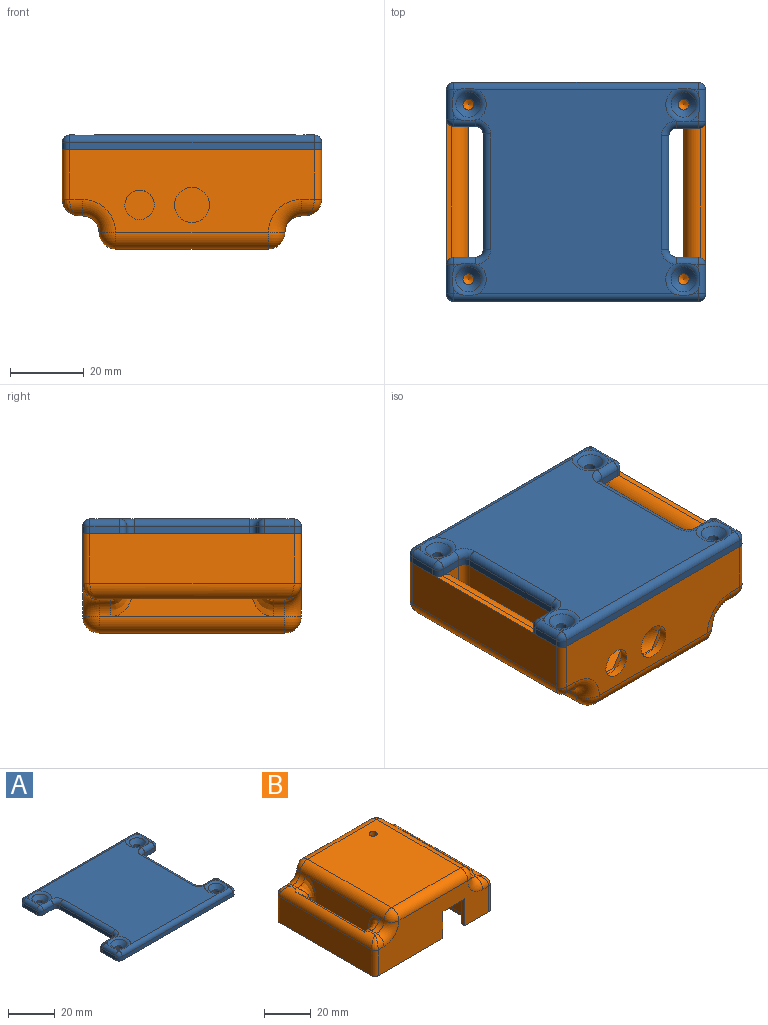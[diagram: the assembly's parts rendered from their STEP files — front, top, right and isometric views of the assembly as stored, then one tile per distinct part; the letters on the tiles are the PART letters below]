
ASSEMBLY  parts=2 mates=1
PART A: 75 faces, bbox 72x61x4 mm
  f0: plane 1.3x1.3mm, normal (0,0,1), area 0.7mm2, adj f72,f73,f74
  f1: plane 1.3x1.3mm, normal (0,0,1), area 0.7mm2, adj f71,f72,f74
  f2: plane 1.3x1.3mm, normal (0,0,1), area 0.7mm2, adj f37,f42,f47
  f3: plane 1.3x1.3mm, normal (0,0,1), area 0.7mm2, adj f37,f41,f42
  f4: plane 1.3x1.3mm, normal (0,0,1), area 0.7mm2, adj f47,f48,f53
  f5: plane 1.3x1.3mm, normal (0,0,1), area 0.7mm2, adj f48,f53,f54
  f6: plane 1.3x1.3mm, normal (0,0,1), area 0.7mm2, adj f62,f69,f73
  f7: plane 2.25x1.8mm, normal (0,0,1), area 1.6mm2, adj f62,f63,f69
  f8: plane 8x2mm, normal (-1,0,0), area 16mm2, adj f21,f39,f45,f48
  f9: plane 66.5x2mm, normal (0,-1,0), area 133mm2, adj f21,f38,f39,f47
  f10: plane 8x2mm, normal (1,0,0), area 16mm2, adj f21,f35,f37,f38
  f11: plane 6x2mm, normal (0,1,0), area 12mm2, adj f21,f35,f40,f41
  f12: plane 31x2mm, normal (1,0,0), area 62mm2, adj f21,f40,f51,f52
  f13: plane 6x2mm, normal (0,-1,0), area 12mm2, adj f21,f50,f51,f63
  f14: plane 8.5x2mm, normal (1,0,0), area 17mm2, adj f21,f50,f61,f62
  f15: plane 66.5x2mm, normal (0,1,0), area 133mm2, adj f21,f60,f61,f73
  f16: plane 8x2mm, normal (-1,0,0), area 16mm2, adj f21,f59,f60,f72
  f17: plane 6x2mm, normal (0,-1,0), area 12mm2, adj f21,f59,f65,f71
  f18: plane 31.5x2mm, normal (-1,0,0), area 63mm2, adj f21,f55,f64,f65
  f19: plane 6x2mm, normal (0,1,0), area 12mm2, adj f21,f45,f54,f55
  f20: plane 55.5x54.12mm, normal (0,0,1), area 2654mm2, adj f42,f46,f47,f52,f53,f57,f58,f63
  f21: plane 70.5x59.5mm, normal (0,0,-1), area 970.3mm2, adj f8,f9,f10,f11,f12,f13,f14,f15
  f22: cylinder r=1.5mm len=3mm, axis (0,0,1), area 14.1mm2, adj f21,f23
  f23: cone r=1.5mm half-angle=45deg, axis (0,0,1), area 41.8mm2, adj f22,f53
  f24: cylinder r=1.5mm len=3mm, axis (0,0,1), area 14.1mm2, adj f21,f25
  f25: cone r=1.5mm half-angle=45deg, axis (0,0,1), area 41.8mm2, adj f24,f42
  f26: cylinder r=1.5mm len=3mm, axis (0,0,1), area 14.1mm2, adj f21,f27
  f27: cone r=1.5mm half-angle=45deg, axis (0,0,1), area 41.8mm2, adj f26,f69
  f28: cylinder r=1.5mm len=3mm, axis (0,0,1), area 14.1mm2, adj f21,f29
  f29: cone r=1.5mm half-angle=45deg, axis (0,0,1), area 41.8mm2, adj f28,f74
  f30: plane 46.5x2mm, normal (0,-1,0), area 93mm2, adj f21,f31,f33,f34
  f31: plane 53.5x2mm, normal (1,0,0), area 107mm2, adj f21,f30,f32,f34
  f32: plane 46.5x2mm, normal (0,1,0), area 93mm2, adj f21,f31,f33,f34
  f33: plane 53.5x2mm, normal (-1,0,0), area 107mm2, adj f21,f30,f32,f34
  f34: plane 53.5x46.5mm, normal (0,0,-1), area 2487.7mm2, adj f30,f31,f32,f33
  f35: cylinder r=2mm len=2mm, axis (0,0,-1), area 6.3mm2, adj f10,f11,f21,f36
  f36: sphere r=2mm, area 6.3mm2, adj f35,f37,f41
  f37: cylinder r=2mm len=8mm, axis (0,-1,0), area 24mm2, adj f2,f3,f10,f36,f42,f43
  f38: cylinder r=2mm len=2mm, axis (0,0,-1), area 6.3mm2, adj f9,f10,f21,f43
  f39: cylinder r=2mm len=2mm, axis (0,0,1), area 6.3mm2, adj f8,f9,f21,f44
  f40: cylinder r=2mm len=2mm, axis (0,0,-1), area 6.3mm2, adj f11,f12,f21,f46
  f41: cylinder r=2mm len=6mm, axis (1,0,0), area 17.4mm2, adj f3,f11,f36,f42,f46
  f42: torus R=4.83mm, axis (0,0,1), area 36mm2, adj f2,f3,f20,f25,f37,f41,f46,f47
  f43: sphere r=2mm, area 6.3mm2, adj f37,f38,f47
  f44: sphere r=2mm, area 6.3mm2, adj f39,f47,f48
  f45: cylinder r=2mm len=2mm, axis (0,0,1), area 6.3mm2, adj f8,f19,f21,f49
  f46: torus R=4mm, axis (0,0,1), area 13.4mm2, adj f20,f40,f41,f42,f52
  f47: cylinder r=2mm len=66.5mm, axis (-1,0,0), area 205.9mm2, adj f2,f4,f9,f20,f42,f43,f44,f53
  f48: cylinder r=2mm len=8mm, axis (0,1,0), area 23.6mm2, adj f4,f5,f8,f44,f49,f53
  f49: sphere r=2mm, area 6.3mm2, adj f45,f48,f54
  f50: cylinder r=2mm len=2mm, axis (0,0,-1), area 6.3mm2, adj f13,f14,f21,f56
  f51: cylinder r=2mm len=2mm, axis (0,0,1), area 6.3mm2, adj f12,f13,f21,f57
  f52: cylinder r=2mm len=31mm, axis (0,-1,0), area 97.4mm2, adj f12,f20,f46,f57
  f53: torus R=4.83mm, axis (0,0,1), area 35.6mm2, adj f4,f5,f20,f23,f47,f48,f54,f58
  f54: cylinder r=2mm len=6mm, axis (1,0,0), area 17.4mm2, adj f5,f19,f49,f53,f58
  f55: cylinder r=2mm len=2mm, axis (0,0,1), area 6.3mm2, adj f18,f19,f21,f58
  f56: sphere r=2mm, area 6.3mm2, adj f50,f62,f63
  f57: torus R=4mm, axis (0,0,1), area 13.5mm2, adj f20,f51,f52,f63
  f58: torus R=4mm, axis (0,0,1), area 13.4mm2, adj f20,f53,f54,f55,f64
  f59: cylinder r=2mm len=2mm, axis (0,0,1), area 6.3mm2, adj f16,f17,f21,f66
  f60: cylinder r=2mm len=2mm, axis (0,0,1), area 6.3mm2, adj f15,f16,f21,f67
  f61: cylinder r=2mm len=2mm, axis (0,0,-1), area 6.3mm2, adj f14,f15,f21,f68
  f62: cylinder r=2mm len=8.5mm, axis (0,-1,0), area 25.6mm2, adj f6,f7,f14,f56,f68,f69
  f63: cylinder r=2mm len=6mm, axis (-1,0,0), area 18.5mm2, adj f7,f13,f20,f56,f57,f69
  f64: cylinder r=2mm len=31.5mm, axis (0,1,0), area 99mm2, adj f18,f20,f58,f70
  f65: cylinder r=2mm len=2mm, axis (0,0,-1), area 6.3mm2, adj f17,f18,f21,f70
  f66: sphere r=2mm, area 6.3mm2, adj f59,f71,f72
  f67: sphere r=2mm, area 6.3mm2, adj f60,f72,f73
  f68: sphere r=2mm, area 6.3mm2, adj f61,f62,f73
  f69: torus R=4.83mm, axis (0,0,1), area 37.2mm2, adj f6,f7,f20,f27,f62,f63,f73
  f70: torus R=4mm, axis (0,0,1), area 13.4mm2, adj f20,f64,f65,f71,f74
  f71: cylinder r=2mm len=6mm, axis (-1,0,0), area 17.4mm2, adj f1,f17,f66,f70,f74
  f72: cylinder r=2mm len=8mm, axis (0,1,0), area 23.6mm2, adj f0,f1,f16,f66,f67,f74
  f73: cylinder r=2mm len=66.5mm, axis (1,0,0), area 205.9mm2, adj f0,f6,f15,f20,f67,f68,f69,f74
  f74: torus R=4.83mm, axis (0,0,1), area 35.6mm2, adj f0,f1,f20,f29,f70,f71,f72,f73
PART B: 123 faces, bbox 70.9x62.5x27.4 mm
  f0: plane 6x2.29mm, normal (0,0,-1), area 4.3mm2, adj f100,f110,f116
  f1: plane 44.5x24mm, normal (0,-1,0), area 796.4mm2, adj f20,f38,f39,f40,f41,f42,f43,f45
  f2: plane 51.5x2mm, normal (-1,0,0), area 103mm2, adj f20,f104,f121,f122
  f3: plane 51.5x2mm, normal (1,0,0), area 103mm2, adj f20,f102,f119,f120
  f4: plane 44.5x24mm, normal (0,1,0), area 842mm2, adj f20,f34,f35,f36,f102,f104,f105,f106
  f5: plane 3x1mm, normal (0,0,1), area 3mm2, adj f60,f63,f66,f72
  f6: plane 3x1mm, normal (0,0,1), area 3mm2, adj f78,f79,f89,f90
  f7: plane 13.5x6.5mm, normal (0,-1,0), area 31.3mm2, adj f20,f33,f52,f64,f95
  f8: plane 13.5x6.5mm, normal (0,1,0), area 31.3mm2, adj f20,f31,f56,f78,f96
  f9: plane 55.5x13.5mm, normal (1,0,0), area 749.2mm2, adj f20,f55,f58,f79
  f10: plane 66.5x22.5mm, normal (0,1,0), area 1184.9mm2, adj f16,f17,f20,f51,f58,f65,f69,f75
  f11: plane 13.5x6.5mm, normal (0,1,0), area 31.3mm2, adj f20,f33,f53,f63,f95
  f12: plane 55.5x13.5mm, normal (-1,0,0), area 749.2mm2, adj f20,f51,f54,f60
  f13: plane 66.5x22.5mm, normal (0,-1,0), area 1124mm2, adj f20,f34,f35,f36,f54,f55,f66,f71
  f14: plane 13.5x6.5mm, normal (0,-1,0), area 31.3mm2, adj f20,f31,f57,f77,f96
  f15: plane 50.5x41.5mm, normal (0,0,1), area 2086.1mm2, adj f80,f81,f91,f92,f97
  f16: cylinder r=4.75mm len=9.5mm, axis (0,1,0), area 59.7mm2, adj f10,f44
  f17: cylinder r=4mm len=8mm, axis (0,1,0), area 50.3mm2, adj f10,f37
  f18: plane 44.89x22.89mm, normal (-1,0,0), area 732.3mm2, adj f20,f52,f53,f67,f68,f80
  f19: plane 44.89x22.89mm, normal (1,0,0), area 731.3mm2, adj f20,f56,f57,f83,f84,f92
  f20: plane 70.5x59.5mm, normal (0,0,-1), area 1050.1mm2, adj f1,f2,f3,f4,f7,f8,f9,f10
  f21: plane 51.5x42.5mm, normal (0,0,-1), area 1957.8mm2, adj f100,f107,f110,f113,f117
  f22: cone r=0mm half-angle=59deg, axis (0,0,-1), area 8.2mm2, adj f23
  f23: cylinder r=1.5mm len=10mm, axis (0,0,-1), area 94.2mm2, adj f20,f22
  f24: cone r=0mm half-angle=59deg, axis (0,0,-1), area 8.2mm2, adj f25
  f25: cylinder r=1.5mm len=10mm, axis (0,0,-1), area 94.2mm2, adj f20,f24
  f26: cone r=0mm half-angle=59deg, axis (0,0,-1), area 8.2mm2, adj f27
  f27: cylinder r=1.5mm len=10mm, axis (0,0,-1), area 94.2mm2, adj f20,f26
  f28: cone r=0mm half-angle=59deg, axis (0,0,-1), area 8.2mm2, adj f29
  f29: cylinder r=1.5mm len=10mm, axis (0,0,-1), area 94.2mm2, adj f20,f28
  f30: plane 3x1mm, normal (0,0,1), area 3mm2, adj f75,f77,f79,f88
  f31: plane 35.5x9mm, normal (-1,0,0), area 319.5mm2, adj f8,f14,f76,f96
  f32: plane 3x1mm, normal (0,0,1), area 3mm2, adj f60,f64,f65,f73
  f33: plane 35.5x9mm, normal (1,0,0), area 319.5mm2, adj f7,f11,f59,f95
  f34: plane 14x2mm, normal (-1,0,0), area 28mm2, adj f4,f13,f20,f35
  f35: plane 13x2mm, normal (0,0,-1), area 26mm2, adj f4,f13,f34,f36
  f36: plane 14x2mm, normal (1,0,0), area 28mm2, adj f4,f13,f20,f35
  f37: plane 11.78x10.2mm, normal (0,-1,0), area 39.8mm2, adj f17,f38,f39,f40,f41,f42,f43
  f38: plane 5.1x2.94mm, normal (0.87,0,0.5), area 11.8mm2, adj f1,f37,f39,f43
  f39: plane 5.89x2mm, normal (0,0,1), area 11.8mm2, adj f1,f37,f38,f40
  f40: plane 5.1x2.94mm, normal (-0.87,0,0.5), area 11.8mm2, adj f1,f37,f39,f41
  f41: plane 5.1x2.94mm, normal (-0.87,0,-0.5), area 11.8mm2, adj f1,f37,f40,f42
  f42: plane 5.89x2mm, normal (0,0,-1), area 11.8mm2, adj f1,f37,f41,f43
  f43: plane 5.1x2.94mm, normal (0.87,0,-0.5), area 11.8mm2, adj f1,f37,f38,f42
  f44: plane 14.09x12.2mm, normal (0,-1,0), area 58mm2, adj f16,f45,f46,f47,f48,f49,f50
  f45: plane 6.1x3.52mm, normal (0.87,0,0.5), area 14.1mm2, adj f1,f44,f46,f50
  f46: plane 7.04x2mm, normal (0,0,1), area 14.1mm2, adj f1,f44,f45,f47
  f47: plane 6.1x3.52mm, normal (-0.87,0,0.5), area 14.1mm2, adj f1,f44,f46,f48
  f48: plane 6.1x3.52mm, normal (-0.87,0,-0.5), area 14.1mm2, adj f1,f44,f47,f49
  f49: plane 7.04x2mm, normal (0,0,-1), area 14.1mm2, adj f1,f44,f48,f50
  f50: plane 6.1x3.52mm, normal (0.87,0,-0.5), area 14.1mm2, adj f1,f44,f45,f49
  f51: cylinder r=2mm len=13.5mm, axis (0,0,1), area 42.4mm2, adj f10,f12,f20,f61
  f52: cylinder r=2mm len=13.5mm, axis (0,0,1), area 42.4mm2, adj f7,f18,f20,f68
  f53: cylinder r=2mm len=13.5mm, axis (0,0,-1), area 42.4mm2, adj f11,f18,f20,f67
  f54: cylinder r=2mm len=13.5mm, axis (0,0,-1), area 42.4mm2, adj f12,f13,f20,f62
  f55: cylinder r=2mm len=13.5mm, axis (0,0,-1), area 42.4mm2, adj f9,f13,f20,f85
  f56: cylinder r=2mm len=13.5mm, axis (0,0,-1), area 42.4mm2, adj f8,f19,f20,f84
  f57: cylinder r=2mm len=13.5mm, axis (0,0,1), area 42.4mm2, adj f14,f19,f20,f83
  f58: cylinder r=2mm len=13.5mm, axis (0,0,1), area 42.4mm2, adj f9,f10,f20,f70
  f59: cylinder r=4.5mm len=41.5mm, axis (0,-1,0), area 213.3mm2, adj f33,f60,f63,f64
  f60: cylinder r=4.5mm len=55.5mm, axis (0,1,0), area 308.9mm2, adj f5,f12,f32,f59,f61,f62,f63,f64
  f61: bspline ~4.71x4.5mm, area 9.8mm2, adj f51,f60,f65
  f62: bspline ~4.71x4.5mm, area 9.8mm2, adj f54,f60,f66
  f63: cylinder r=4.5mm len=5mm, axis (1,0,0), area 14.6mm2, adj f5,f11,f59,f60,f67
  f64: cylinder r=4.5mm len=5mm, axis (-1,0,0), area 14.6mm2, adj f7,f32,f59,f60,f68
  f65: cylinder r=4.5mm len=4.5mm, axis (1,0,0), area 18.3mm2, adj f10,f32,f61,f69
  f66: cylinder r=4.5mm len=4.5mm, axis (-1,0,0), area 18.3mm2, adj f5,f13,f62,f71
  f67: bspline ~9x6.5mm, area 45.2mm2, adj f18,f53,f63,f72
  f68: bspline ~9x6.5mm, area 45.2mm2, adj f18,f52,f64,f73
  f69: torus R=9mm, axis (0,-1,0), area 68.1mm2, adj f10,f65,f73,f74
  f70: bspline ~4.71x4.5mm, area 9.8mm2, adj f58,f75,f79
  f71: torus R=9mm, axis (0,-1,0), area 68.1mm2, adj f13,f66,f72,f86
  f72: cylinder r=4.5mm len=4.5mm, axis (0,-1,0), area 21.2mm2, adj f5,f67,f71,f80
  f73: cylinder r=4.5mm len=4.5mm, axis (0,1,0), area 21.2mm2, adj f32,f68,f69,f80
  f74: sphere r=4.5mm, area 43.4mm2, adj f69,f80,f81
  f75: cylinder r=4.5mm len=4.5mm, axis (1,0,0), area 18.3mm2, adj f10,f30,f70,f82
  f76: cylinder r=4.5mm len=41.5mm, axis (0,-1,0), area 213.3mm2, adj f31,f77,f78,f79
  f77: cylinder r=4.5mm len=5mm, axis (-1,0,0), area 14.6mm2, adj f14,f30,f76,f79,f83
  f78: cylinder r=4.5mm len=5mm, axis (1,0,0), area 14.6mm2, adj f6,f8,f76,f79,f84
  f79: cylinder r=4.5mm len=55.5mm, axis (0,1,0), area 308.9mm2, adj f6,f9,f30,f70,f76,f77,f78,f85
  f80: cylinder r=4.5mm len=50.5mm, axis (0,1,0), area 357mm2, adj f15,f18,f72,f73,f74,f86
  f81: cylinder r=4.5mm len=41.5mm, axis (1,0,0), area 293.3mm2, adj f10,f15,f74,f87
  f82: torus R=9mm, axis (0,-1,0), area 68.1mm2, adj f10,f75,f87,f88
  f83: bspline ~9x6.5mm, area 45.2mm2, adj f19,f57,f77,f88
  f84: bspline ~9x6.5mm, area 45.2mm2, adj f19,f56,f78,f89
  f85: bspline ~4.71x4.5mm, area 9.8mm2, adj f55,f79,f90
  f86: sphere r=4.5mm, area 31.8mm2, adj f71,f80,f91
  f87: sphere r=4.5mm, area 20.2mm2, adj f81,f82,f92
  f88: cylinder r=4.5mm len=4.5mm, axis (0,-1,0), area 21.2mm2, adj f30,f82,f83,f92
  f89: cylinder r=4.5mm len=4.5mm, axis (0,1,0), area 21.2mm2, adj f6,f84,f92,f93
  f90: cylinder r=4.5mm len=4.5mm, axis (-1,0,0), area 18.3mm2, adj f6,f13,f85,f93
  f91: cylinder r=4.5mm len=41.5mm, axis (-1,0,0), area 293.3mm2, adj f13,f15,f86,f94
  f92: cylinder r=4.5mm len=50.5mm, axis (0,-1,0), area 357mm2, adj f15,f19,f87,f88,f89,f94
  f93: torus R=9mm, axis (0,-1,0), area 68.1mm2, adj f13,f89,f90,f94
  f94: sphere r=4.5mm, area 31.8mm2, adj f91,f92,f93
  f95: cylinder r=4.5mm len=35.5mm, axis (0,1,0), area 250.9mm2, adj f7,f11,f20,f33
  f96: cylinder r=4.5mm len=35.5mm, axis (0,1,0), area 250.9mm2, adj f8,f14,f20,f31
  f97: cylinder r=1.75mm len=17mm, axis (0,0,1), area 186.9mm2, adj f15,f99
  f98: cylinder r=4mm len=10mm, axis (0,0,1), area 251.3mm2, adj f99,f100
  f99: plane 8x8mm, normal (0,0,-1), area 40.6mm2, adj f97,f98
  f100: torus R=9mm, axis (0,0,1), area 251.1mm2, adj f0,f21,f98,f118
  f101: plane 51.5x22mm, normal (1,0,0), area 1133mm2, adj f102,f106,f112,f113
  f102: plane 53.5x2mm, normal (0,0,-1), area 53.5mm2, adj f1,f3,f4,f101,f106,f112,f119,f120
  f103: plane 51.5x22mm, normal (-1,0,0), area 1133mm2, adj f104,f105,f110,f111
  f104: plane 53.5x2mm, normal (0,0,-1), area 53.5mm2, adj f1,f2,f4,f103,f105,f111,f121,f122
  f105: cylinder r=1mm len=22mm, axis (0,0,-1), area 34.6mm2, adj f4,f103,f104,f108
  f106: cylinder r=1mm len=22mm, axis (0,0,-1), area 34.6mm2, adj f4,f101,f102,f109
  f107: cylinder r=1mm len=42.5mm, axis (1,0,0), area 66.8mm2, adj f4,f21,f108,f109
  f108: sphere r=1mm, area 1.6mm2, adj f105,f107,f110
  f109: sphere r=1mm, area 1.6mm2, adj f106,f107,f113
  f110: cylinder r=1mm len=51.5mm, axis (0,-1,0), area 80.9mm2, adj f0,f21,f103,f108,f114
  f111: cylinder r=1mm len=22mm, axis (0,0,1), area 34.6mm2, adj f1,f103,f104,f114
  f112: cylinder r=1mm len=22mm, axis (0,0,1), area 34.6mm2, adj f1,f101,f102,f115
  f113: cylinder r=1mm len=51.5mm, axis (0,1,0), area 80.9mm2, adj f21,f101,f109,f115
  f114: sphere r=1mm, area 1mm2, adj f110,f111,f116
  f115: sphere r=1mm, area 2.1mm2, adj f112,f113,f117
  f116: cylinder r=1mm len=2.29mm, axis (-1,0,0), area 3.6mm2, adj f0,f1,f114,f118
  f117: cylinder r=1mm len=26.79mm, axis (-1,0,0), area 42.1mm2, adj f1,f21,f115,f118
  f118: bspline ~16.53x2.65mm, area 27.7mm2, adj f1,f100,f116,f117
  f119: cylinder r=1mm len=2mm, axis (0,0,-1), area 3.1mm2, adj f1,f3,f20,f102
  f120: cylinder r=1mm len=2mm, axis (0,0,1), area 3.1mm2, adj f3,f4,f20,f102
  f121: cylinder r=1mm len=2mm, axis (0,0,1), area 3.1mm2, adj f2,f4,f20,f104
  f122: cylinder r=1mm len=2mm, axis (0,0,-1), area 3.1mm2, adj f1,f2,f20,f104
PLACE A t=(17.37,31.99,19.61)mm
PLACE B rot(axis=(1,0,0),180deg) t=(17.87,31.74,19.61)mm
MATE fastened B.f22 <-> A.f28  axis (0,0,1) through (-11.38,54.49,19.61)mm
